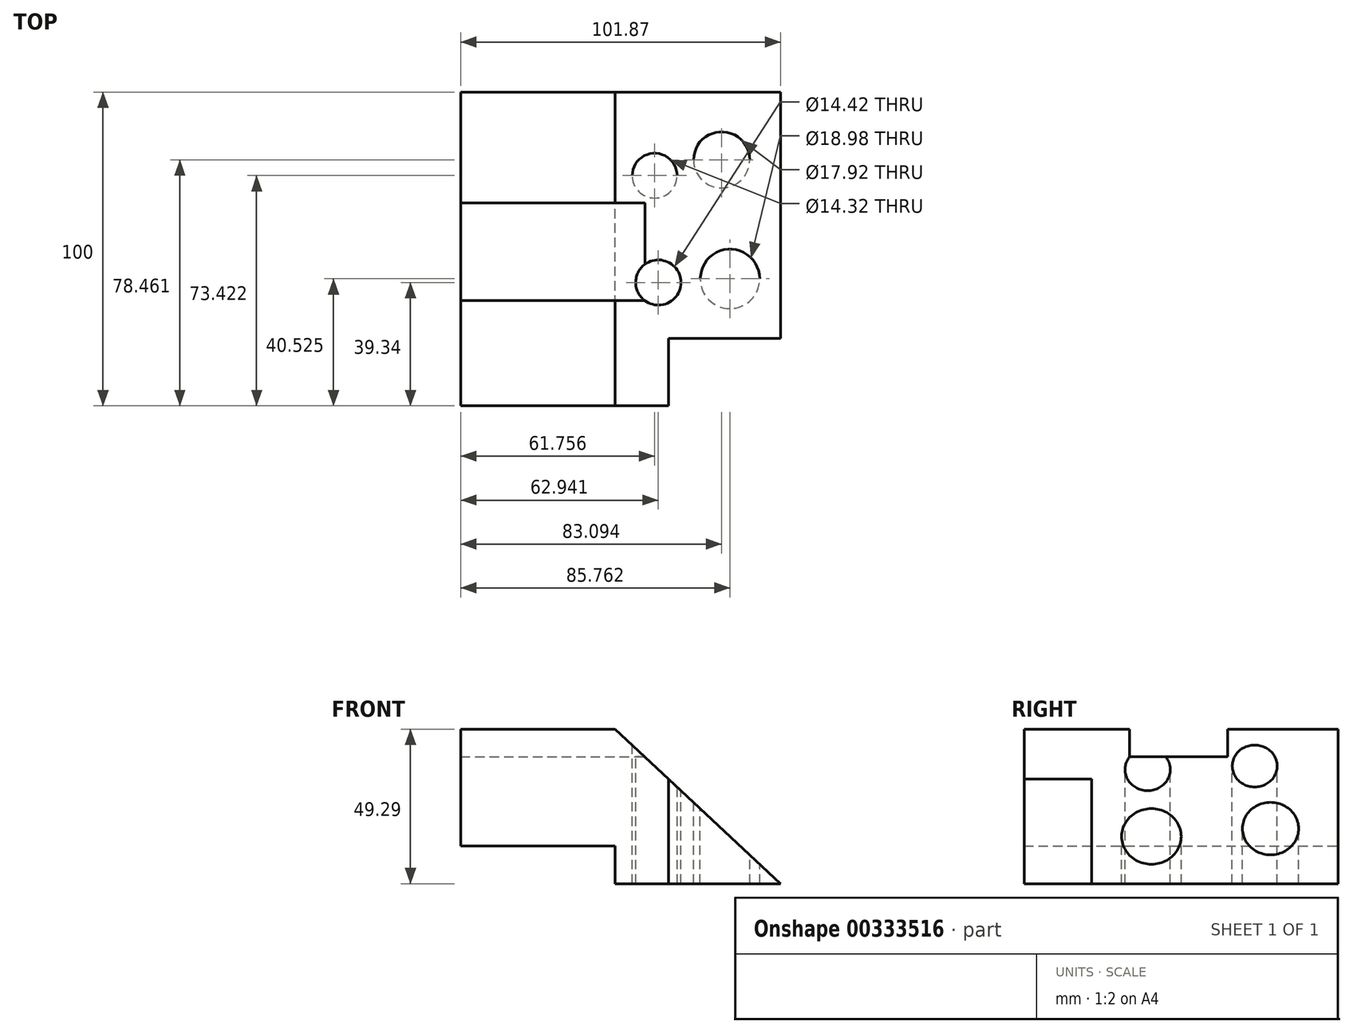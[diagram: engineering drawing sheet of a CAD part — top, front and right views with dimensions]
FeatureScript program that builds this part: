
annotation { "Feature Type Name" : "Feature", "Feature Type Description" : "" }
export const myFeature = defineFeature(function(context is Context, id is Id, definition is map)
    precondition{}
    {
        {
            var Q0;
            Q0=qCreatedBy(makeId("Front.planeOp"),FACE);
            var sketch = newSketch(context, id + "F0", { "sketchPlane" : qUnion([Q0])});
            skLineSegment(sketch, "E0", {"start": v(-49.16, 0) * mm, "end": v(0, 0) * mm});
            skLineSegment(sketch, "E1", {"start": v(0, 0) * mm, "end": v(0, -12.07) * mm});
            skLineSegment(sketch, "E2", {"start": v(0, -12.07) * mm, "end": v(52.71, -12.07) * mm});
            skLineSegment(sketch, "E3", {"start": v(52.71, -12.07) * mm, "end": v(0, 37.22) * mm});
            skLineSegment(sketch, "E4", {"start": v(0, 37.22) * mm, "end": v(-49.16, 37.22) * mm});
            skLineSegment(sketch, "E5", {"start": v(-49.16, 37.22) * mm, "end": v(-49.16, 0) * mm});
            skSolve(sketch);
        }
        {
            var Q0;
            Q0=makeQuery(id+"F0.imprint","IMPRINT",FACE,{"disambiguationData":[TD([[makeQuery(id+"F0.imprint","IMPRINT",EDGE,{"derivedFrom":sQuery(id+"F0.wireOp",EDGE,"E0")}),1.0]])]});
            extrude(context, id + "F1", {"entities" : qUnion([Q0]), "depth" : 100 * mm, "offsetDistance" : 25 * mm});
        }
        {
            var Q0;
            Q0=qCreatedBy(makeId("Top.planeOp"),FACE);
            var sketch = newSketch(context, id + "F2", { "sketchPlane" : qUnion([Q0])});
            skLineSegment(sketch, "E6.bottom", {"start": v(17.04, -100.37) * mm, "end": v(55.27, -100.37) * mm});
            skLineSegment(sketch, "E6.top", {"start": v(17.04, -78.44) * mm, "end": v(55.27, -78.44) * mm});
            skLineSegment(sketch, "E6.left", {"start": v(17.04, -100.37) * mm, "end": v(17.04, -78.44) * mm});
            skLineSegment(sketch, "E6.right", {"start": v(55.27, -100.37) * mm, "end": v(55.27, -78.44) * mm});
            skSolve(sketch);
        }
        {
            var Q0;
            Q0=makeQuery(id+"F2.imprint","IMPRINT",FACE,{"disambiguationData":[TD([[makeQuery(id+"F2.imprint","IMPRINT",EDGE,{"derivedFrom":sQuery(id+"F2.wireOp",EDGE,"E6.bottom")}),1.0]])]});
            extrude(context, id + "F3", {"entities" : qUnion([Q0]), "operationType" : NewBodyOperationType.REMOVE, "oppositeDirection" : true, "depth" : 75 * mm, "offsetDistance" : 25 * mm, "symmetric" : true});
        }
        {
            var Q0;
            Q0=qCreatedBy(makeId("Right.planeOp"),FACE);
            var sketch = newSketch(context, id + "F4", { "sketchPlane" : qUnion([Q0])});
            skLineSegment(sketch, "E7.bottom", {"start": v(-35.24, 39.76) * mm, "end": v(-66.4, 39.76) * mm});
            skLineSegment(sketch, "E7.top", {"start": v(-35.24, 28.35) * mm, "end": v(-66.4, 28.35) * mm});
            skLineSegment(sketch, "E7.left", {"start": v(-35.24, 39.76) * mm, "end": v(-35.24, 28.35) * mm});
            skLineSegment(sketch, "E7.right", {"start": v(-66.4, 39.76) * mm, "end": v(-66.4, 28.35) * mm});
            skSolve(sketch);
        }
        {
            var Q0;
            Q0 = qSketchRegion(id + "F4", true);
            extrude(context, id + "F5", {"entities" : qUnion([Q0]), "operationType" : NewBodyOperationType.REMOVE, "oppositeDirection" : true, "depth" : 200 * mm, "offsetDistance" : 25 * mm, "symmetric" : true});
        }
        {
            var Q0;
            Q0=qCreatedBy(makeId("Top.planeOp"),FACE);
            var sketch = newSketch(context, id + "F6", { "sketchPlane" : qUnion([Q0])});
            skCircle(sketch, "E8", {"center": v(13.78, -60.66) * mm, "radius": 7.21 * mm});
            skCircle(sketch, "E9", {"center": v(36.6, -59.47) * mm, "radius": 9.49 * mm});
            skCircle(sketch, "E10", {"center": v(33.93, -21.54) * mm, "radius": 8.96 * mm});
            skCircle(sketch, "E11", {"center": v(12.6, -26.58) * mm, "radius": 7.16 * mm});
            skSolve(sketch);
        }
        {
            var Q0;
            Q0 = qSketchRegion(id + "F6", true);
            extrude(context, id + "F7", {"entities" : qUnion([Q0]), "operationType" : NewBodyOperationType.REMOVE, "oppositeDirection" : true, "depth" : 5000 * mm, "offsetDistance" : 25 * mm, "symmetric" : true});
        }
    });
